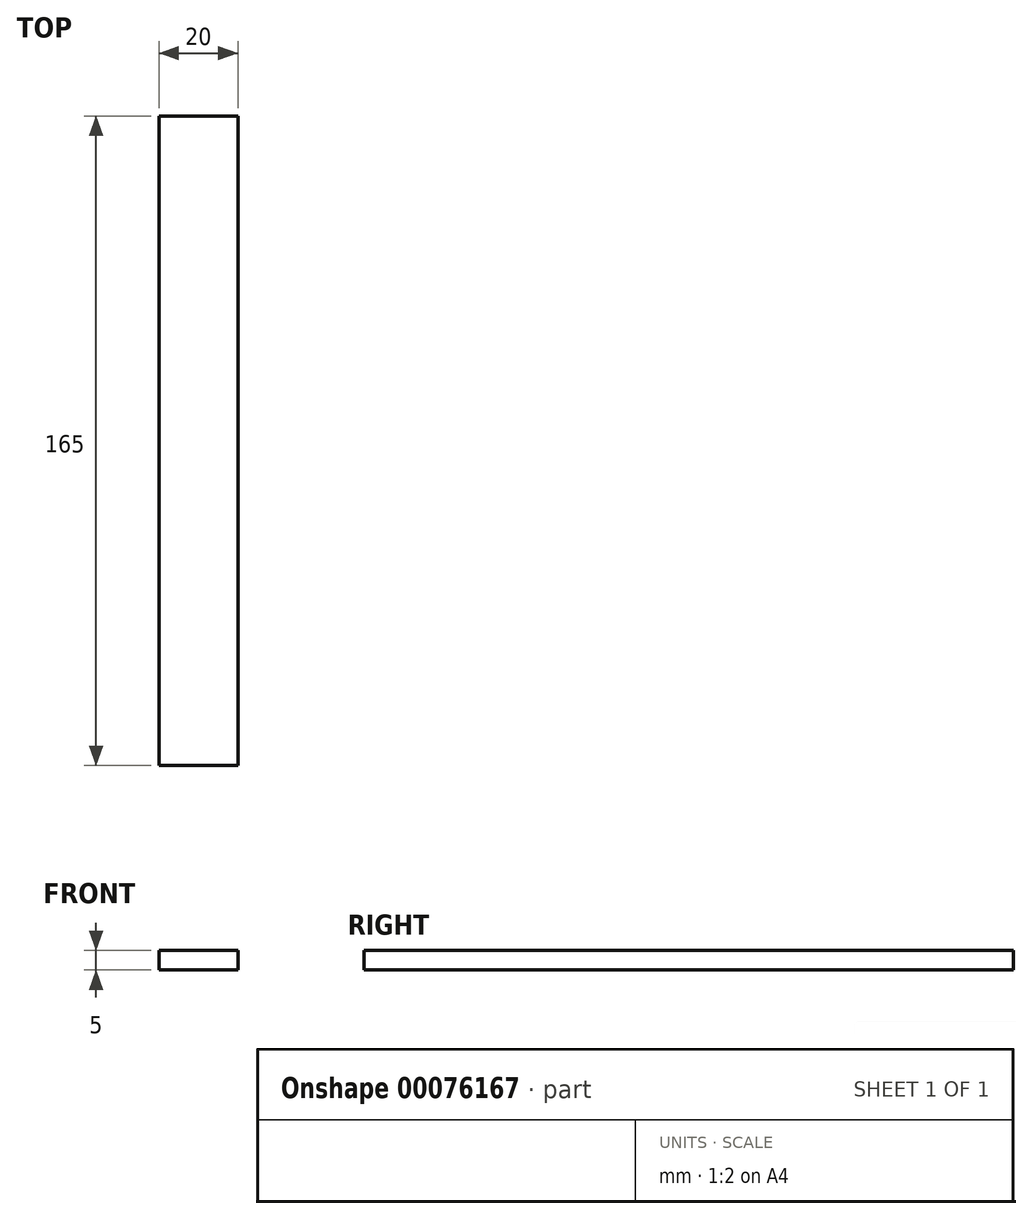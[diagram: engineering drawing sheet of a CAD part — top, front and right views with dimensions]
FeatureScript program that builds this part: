
annotation { "Feature Type Name" : "Feature", "Feature Type Description" : "" }
export const myFeature = defineFeature(function(context is Context, id is Id, definition is map)
    precondition{}
    {
        {
            var Q0;
            Q0=qCreatedBy(makeId("Top.planeOp"),FACE);
            var sketch = newSketch(context, id + "F0", { "sketchPlane" : qUnion([Q0])});
            skLineSegment(sketch, "E0.bottom", {"start": v(0, 0) * mm, "end": v(20, 0) * mm});
            skLineSegment(sketch, "E0.top", {"start": v(0, 165) * mm, "end": v(20, 165) * mm});
            skLineSegment(sketch, "E0.left", {"start": v(0, 0) * mm, "end": v(0, 165) * mm});
            skLineSegment(sketch, "E0.right", {"start": v(20, 0) * mm, "end": v(20, 165) * mm});
            skSolve(sketch);
        }
        {
            var Q0;
            Q0=makeQuery(id+"F0.imprint","IMPRINT",FACE,{"disambiguationData":[TD([[makeQuery(id+"F0.imprint","IMPRINT",EDGE,{"derivedFrom":sQuery(id+"F0.wireOp",EDGE,"E0.bottom")}),1.0]])]});
            extrude(context, id + "F1", {"entities" : qUnion([Q0]), "depth" : 5 * mm});
        }
    });
